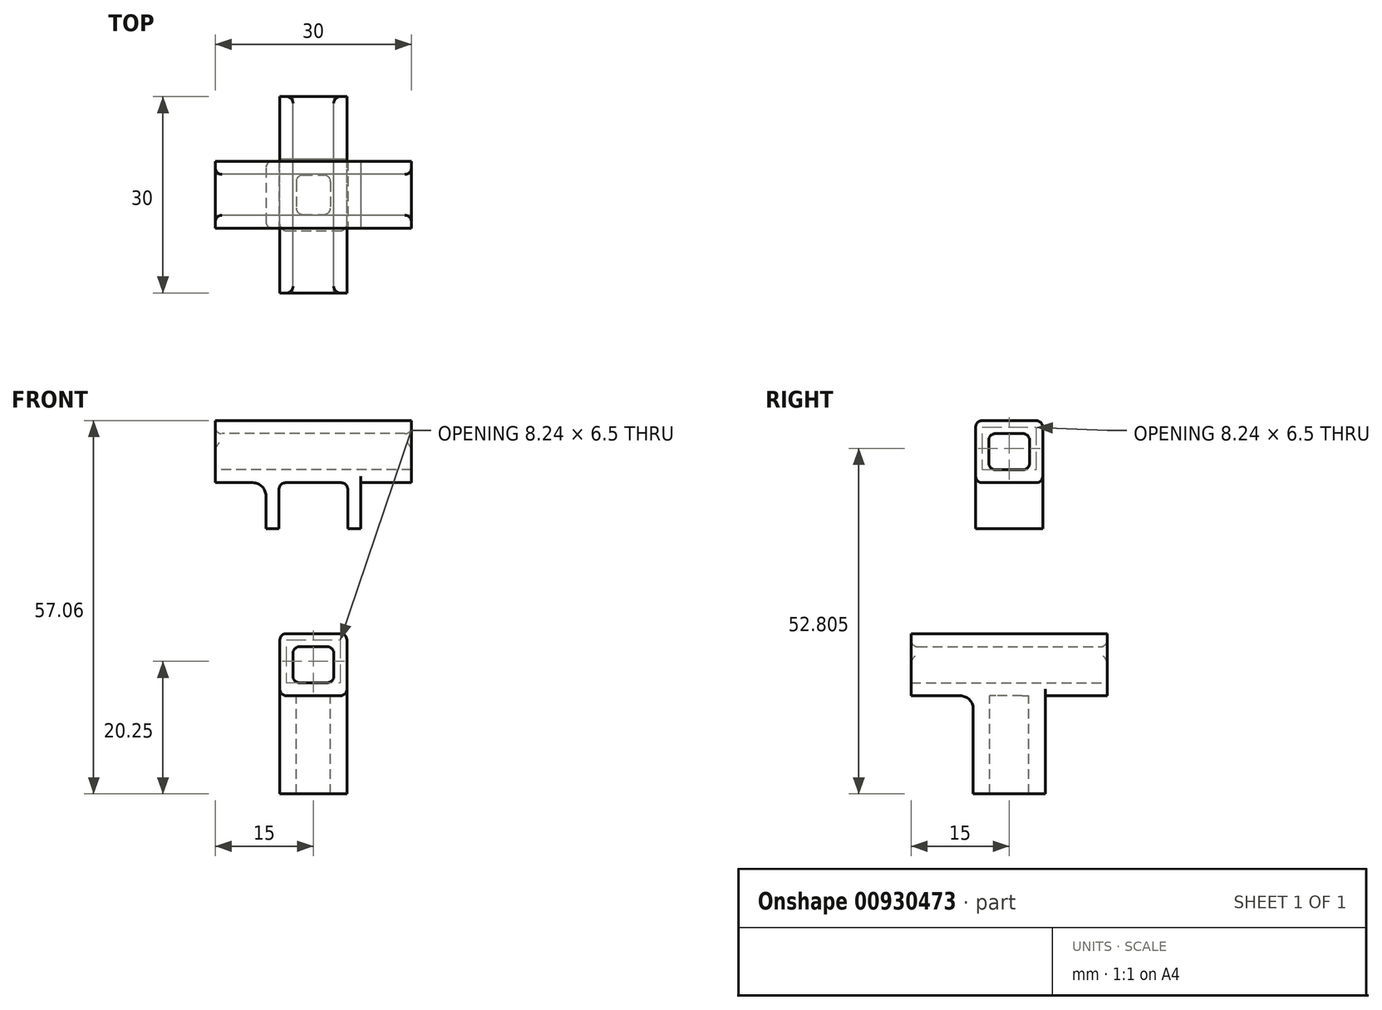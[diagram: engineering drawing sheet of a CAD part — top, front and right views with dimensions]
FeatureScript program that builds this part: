
annotation { "Feature Type Name" : "Feature", "Feature Type Description" : "" }
export const myFeature = defineFeature(function(context is Context, id is Id, definition is map)
    precondition{}
    {
        {
            var Q0;
            Q0=qCreatedBy(makeId("Front.planeOp"),FACE);
            var sketch = newSketch(context, id + "F0", { "sketchPlane" : qUnion([Q0])});
            skLineSegment(sketch, "E0.bottom", {"start": v(3.13, -2.75) * mm, "end": v(-3.12, -2.75) * mm});
            skLineSegment(sketch, "E0.top", {"start": v(3.12, 2.75) * mm, "end": v(-3.13, 2.75) * mm});
            skLineSegment(sketch, "E0.left", {"start": v(3.13, -2.75) * mm, "end": v(3.12, 2.75) * mm});
            skLineSegment(sketch, "E0.right", {"start": v(-3.12, -2.75) * mm, "end": v(-3.13, 2.75) * mm});
            skPoint(sketch, "E0.middle", {"position": v(0, 0) * mm});
            skLineSegment(sketch, "E1.0", {"start": v(5.12, 4.75) * mm, "end": v(-5.12, 4.75) * mm});
            skLineSegment(sketch, "E1.1", {"start": v(5.12, -4.75) * mm, "end": v(5.12, 4.75) * mm});
            skLineSegment(sketch, "E1.2", {"start": v(5.12, -4.75) * mm, "end": v(-5.12, -4.75) * mm});
            skLineSegment(sketch, "E1.3", {"start": v(-5.12, -4.75) * mm, "end": v(-5.12, 4.75) * mm});
            skSolve(sketch);
        }
        {
            var Q0;
            Q0=makeQuery(id+"F0.imprint","IMPRINT",FACE,{"disambiguationData":[TD([[makeQuery(id+"F0.imprint","IMPRINT",EDGE,{"derivedFrom":sQuery(id+"F0.wireOp",EDGE,"E0.bottom")}),1.0]])]});
            extrude(context, id + "F1", {"entities" : qUnion([Q0]), "endBound" : BoundingType.SYMMETRIC, "depth" : 30 * mm, "offsetDistance" : 25 * mm});
        }
        {
            var Q0;
            Q0=qCreatedBy(makeId("Right.planeOp"),FACE);
            var sketch = newSketch(context, id + "F2", { "sketchPlane" : qUnion([Q0])});
            skLineSegment(sketch, "E2.bottom", {"start": v(3.13, 4.8) * mm, "end": v(-3.13, 4.8) * mm});
            skLineSegment(sketch, "E2.top", {"start": v(3.13, 10.3) * mm, "end": v(-3.13, 10.3) * mm});
            skLineSegment(sketch, "E2.left", {"start": v(3.13, 4.8) * mm, "end": v(3.13, 10.3) * mm});
            skLineSegment(sketch, "E2.right", {"start": v(-3.13, 4.8) * mm, "end": v(-3.13, 10.3) * mm});
            skPoint(sketch, "E2.middle", {"position": v(0, 7.56) * mm});
            skLineSegment(sketch, "E3.0", {"start": v(5.13, 12.3) * mm, "end": v(-5.13, 12.3) * mm});
            skLineSegment(sketch, "E3.1", {"start": v(5.13, 2.8) * mm, "end": v(5.13, 12.3) * mm});
            skLineSegment(sketch, "E3.2", {"start": v(5.13, 2.8) * mm, "end": v(-5.13, 2.8) * mm});
            skLineSegment(sketch, "E3.3", {"start": v(-5.13, 2.8) * mm, "end": v(-5.13, 12.3) * mm});
            skSolve(sketch);
        }
        {
            var Q0;
            Q0=makeQuery(id+"F2.imprint","IMPRINT",FACE,{"disambiguationData":[TD([[makeQuery(id+"F2.imprint","IMPRINT",EDGE,{"derivedFrom":sQuery(id+"F2.wireOp",EDGE,"E2.bottom")}),1.0]])]});
            extrude(context, id + "F3", {"entities" : qUnion([Q0]), "endBound" : BoundingType.SYMMETRIC, "depth" : 30 * mm, "offsetDistance" : 25 * mm});
        }
        {
            var Q0;
            Q0=makeQuery(id+"F3.opExtrude","SWEPT_FACE",FACE,{"disambiguationData":[OSD([sQuery(id+"F2.wireOp",EDGE,"E3.2")])]});
            var sketch = newSketch(context, id + "F4", { "sketchPlane" : qUnion([Q0])});
            skLineSegment(sketch, "E4", {"start": v(0, 0) * mm, "end": v(-5.25, 0) * mm, "construction": true});
            skLineSegment(sketch, "E5.MirrorCS", {"start": v(0, 0) * mm, "end": v(5.25, 0) * mm, "construction": true});
            skLineSegment(sketch, "E6.bottom", {"start": v(-5.25, -5.13) * mm, "end": v(-7.25, -5.13) * mm});
            skLineSegment(sketch, "E6.top", {"start": v(-5.25, 5.13) * mm, "end": v(-7.25, 5.13) * mm});
            skLineSegment(sketch, "E6.left", {"start": v(-5.25, -5.13) * mm, "end": v(-5.25, 5.13) * mm});
            skLineSegment(sketch, "E6.right", {"start": v(-7.25, -5.13) * mm, "end": v(-7.25, 5.13) * mm});
            skLineSegment(sketch, "E7.MirrorCS", {"start": v(5.25, -5.13) * mm, "end": v(5.25, 5.13) * mm});
            skLineSegment(sketch, "E8.MirrorCS", {"start": v(7.25, -5.13) * mm, "end": v(7.25, 5.13) * mm});
            skLineSegment(sketch, "E9.MirrorCS", {"start": v(5.25, 5.13) * mm, "end": v(7.25, 5.13) * mm});
            skLineSegment(sketch, "E10.MirrorCS", {"start": v(5.25, -5.13) * mm, "end": v(7.25, -5.13) * mm});
            skSolve(sketch);
        }
        {
            var Q0;
            Q0=makeQuery(id+"F4.imprint","IMPRINT",FACE,{"disambiguationData":[TD([[makeQuery(id+"F4.imprint","IMPRINT",EDGE,{"derivedFrom":sQuery(id+"F4.wireOp",EDGE,"E6.top")}),1.0]])]});
            var Q1;
            Q1=makeQuery(id+"F4.imprint","IMPRINT",FACE,{"disambiguationData":[TD([[makeQuery(id+"F4.imprint","IMPRINT",EDGE,{"derivedFrom":sQuery(id+"F4.wireOp",EDGE,"E7.MirrorCS")}),-1.0]])]});
            extrude(context, id + "F5", {"entities" : qUnion([Q0, Q1]), "operationType" : NewBodyOperationType.ADD, "depth" : 7 * mm, "offsetDistance" : 25 * mm});
        }
        {
            var Q0;
            Q0=makeQuery(id+"F1.opExtrude","SWEPT_FACE",FACE,{"disambiguationData":[OSD([sQuery(id+"F0.wireOp",EDGE,"E1.2")])]});
            var sketch = newSketch(context, id + "F6", { "sketchPlane" : qUnion([Q0])});
            skLineSegment(sketch, "E11.bottom", {"start": v(-2.62, -3) * mm, "end": v(2.63, -3) * mm});
            skLineSegment(sketch, "E11.top", {"start": v(-2.63, 3) * mm, "end": v(2.62, 3) * mm});
            skLineSegment(sketch, "E11.left", {"start": v(-2.62, -3) * mm, "end": v(-2.63, 3) * mm});
            skLineSegment(sketch, "E11.right", {"start": v(2.63, -3) * mm, "end": v(2.62, 3) * mm});
            skPoint(sketch, "E11.middle", {"position": v(0, 0) * mm});
            skLineSegment(sketch, "E12.0", {"start": v(-5.12, -5.5) * mm, "end": v(5.12, -5.5) * mm});
            skLineSegment(sketch, "E12.1", {"start": v(-5.12, -5.5) * mm, "end": v(-5.13, 5.5) * mm});
            skLineSegment(sketch, "E12.2", {"start": v(-5.13, 5.5) * mm, "end": v(5.12, 5.5) * mm});
            skLineSegment(sketch, "E12.3", {"start": v(5.12, -5.5) * mm, "end": v(5.12, 5.5) * mm});
            skSolve(sketch);
        }
        {
            var Q0;
            Q0=makeQuery(id+"F6.imprint","IMPRINT",FACE,{"disambiguationData":[TD([[makeQuery(id+"F6.imprint","IMPRINT",EDGE,{"derivedFrom":sQuery(id+"F6.wireOp",EDGE,"E11.bottom")}),-1.0]])]});
            extrude(context, id + "F7", {"entities" : qUnion([Q0]), "operationType" : NewBodyOperationType.ADD, "depth" : 15 * mm, "offsetDistance" : 25 * mm});
        }
        {
            var Q0;
            Q0=makeQuery(id+"F5.opExtrude","CAP_EDGE",EDGE,{"disambiguationData":[OSD([sQuery(id+"F4.wireOp",EDGE,"E8.MirrorCS")])],"isStart":true});
            var Q1;
            Q1=makeQuery(id+"F5.opExtrude","CAP_EDGE",EDGE,{"disambiguationData":[OSD([sQuery(id+"F4.wireOp",EDGE,"E6.right")])],"isStart":true});
            fillet(context, id + "F8", {"entities" : qUnion([Q0, Q1]), "radius" : 2 * mm, "tangentPropagation" : true, "allowEdgeOverflow" : false});
        }
        {
            var Q0;
            Q0=makeQuery(id+"F7.opExtrude","CAP_EDGE",EDGE,{"disambiguationData":[OSD([sQuery(id+"F6.wireOp",EDGE,"E12.2")])],"isStart":true});
            var Q1;
            Q1=makeQuery(id+"F7.opExtrude","CAP_EDGE",EDGE,{"disambiguationData":[OSD([sQuery(id+"F6.wireOp",EDGE,"E12.0")])],"isStart":true});
            fillet(context, id + "F9", {"entities" : qUnion([Q0, Q1]), "radius" : 2 * mm, "tangentPropagation" : true, "allowEdgeOverflow" : false});
        }
        {
            var Q0;
            Q0=makeQuery(id+"F3.opExtrude","SWEPT_EDGE",EDGE,{"disambiguationData":[OSD([sQuery(id+"F2.wireOp",EDGE,"E2.top"),sQuery(id+"F2.wireOp",EDGE,"E2.right")])]});
            var Q1;
            Q1=makeQuery(id+"F3.opExtrude","SWEPT_EDGE",EDGE,{"disambiguationData":[OSD([sQuery(id+"F2.wireOp",EDGE,"E2.bottom"),sQuery(id+"F2.wireOp",EDGE,"E2.left")])]});
            var Q2;
            Q2=makeQuery(id+"F3.opExtrude","SWEPT_EDGE",EDGE,{"disambiguationData":[OSD([sQuery(id+"F2.wireOp",EDGE,"E2.bottom"),sQuery(id+"F2.wireOp",EDGE,"E2.right")])]});
            var Q3;
            Q3=makeQuery(id+"F3.opExtrude","SWEPT_EDGE",EDGE,{"disambiguationData":[OSD([sQuery(id+"F2.wireOp",EDGE,"E2.top"),sQuery(id+"F2.wireOp",EDGE,"E2.left")])]});
            var Q4;
            Q4=makeQuery(id+"F1.opExtrude","SWEPT_EDGE",EDGE,{"disambiguationData":[OSD([sQuery(id+"F0.wireOp",EDGE,"E0.top"),sQuery(id+"F0.wireOp",EDGE,"E0.left")])]});
            var Q5;
            Q5=makeQuery(id+"F1.opExtrude","SWEPT_EDGE",EDGE,{"disambiguationData":[OSD([sQuery(id+"F0.wireOp",EDGE,"E0.top"),sQuery(id+"F0.wireOp",EDGE,"E0.right")])]});
            var Q6;
            Q6=makeQuery(id+"F1.opExtrude","SWEPT_EDGE",EDGE,{"disambiguationData":[OSD([sQuery(id+"F0.wireOp",EDGE,"E0.bottom"),sQuery(id+"F0.wireOp",EDGE,"E0.right")])]});
            var Q7;
            Q7=makeQuery(id+"F1.opExtrude","SWEPT_EDGE",EDGE,{"disambiguationData":[OSD([sQuery(id+"F0.wireOp",EDGE,"E0.bottom"),sQuery(id+"F0.wireOp",EDGE,"E0.left")])]});
            var Q8;
            Q8=makeQuery(id+"F3.opExtrude","CAP_EDGE",EDGE,{"disambiguationData":[OSD([sQuery(id+"F2.wireOp",EDGE,"E2.top")])],"isStart":false});
            var Q9;
            Q9=makeQuery(id+"F3.opExtrude","CAP_EDGE",EDGE,{"disambiguationData":[OSD([sQuery(id+"F2.wireOp",EDGE,"E2.top")])],"isStart":true});
            var Q10;
            Q10=makeQuery(id+"F1.opExtrude","CAP_EDGE",EDGE,{"disambiguationData":[OSD([sQuery(id+"F0.wireOp",EDGE,"E0.top")])],"isStart":false});
            var Q11;
            Q11=makeQuery(id+"F1.opExtrude","CAP_EDGE",EDGE,{"disambiguationData":[OSD([sQuery(id+"F0.wireOp",EDGE,"E0.top")])],"isStart":true});
            fillet(context, id + "F10", {"entities" : qUnion([Q0, Q1, Q2, Q3, Q4, Q5, Q6, Q7, Q8, Q9, Q10, Q11]), "radius" : 1 * mm, "tangentPropagation" : true, "allowEdgeOverflow" : false});
        }
        {
            var Q0;
            Q0=makeQuery(id+"F3.opExtrude","SWEPT_EDGE",EDGE,{"disambiguationData":[OSD([sQuery(id+"F2.wireOp",EDGE,"E3.0"),sQuery(id+"F2.wireOp",EDGE,"E3.1")])]});
            var Q1;
            Q1=makeQuery(id+"F3.opExtrude","SWEPT_EDGE",EDGE,{"disambiguationData":[OSD([sQuery(id+"F2.wireOp",EDGE,"E3.0"),sQuery(id+"F2.wireOp",EDGE,"E3.3")])]});
            var Q2;
            Q2=makeQuery(id+"F1.opExtrude","SWEPT_EDGE",EDGE,{"disambiguationData":[OSD([sQuery(id+"F0.wireOp",EDGE,"E1.0"),sQuery(id+"F0.wireOp",EDGE,"E1.3")])]});
            var Q3;
            Q3=makeQuery(id+"F1.opExtrude","SWEPT_EDGE",EDGE,{"disambiguationData":[OSD([sQuery(id+"F0.wireOp",EDGE,"E1.0"),sQuery(id+"F0.wireOp",EDGE,"E1.1")])]});
            var Q4;
            Q4=makeQuery(id+"F5.opExtrude","CAP_EDGE",EDGE,{"disambiguationData":[OSD([sQuery(id+"F4.wireOp",EDGE,"E6.left")])],"isStart":true});
            var Q5;
            Q5=makeQuery(id+"F5.opExtrude","CAP_EDGE",EDGE,{"disambiguationData":[OSD([sQuery(id+"F4.wireOp",EDGE,"E7.MirrorCS")])],"isStart":true});
            fillet(context, id + "F11", {"entities" : qUnion([Q0, Q1, Q2, Q3, Q4, Q5]), "radius" : 1 * mm, "tangentPropagation" : true, "allowEdgeOverflow" : false});
        }
        {
            var Q0;
            {var subQ0=sQuery(id+"F2.wireOp",EDGE,"E3.2");var subQ1=sQuery(id+"F2.wireOp",EDGE,"E3.1");Q0=makeQuery(id+"F5.boolean.opBoolean","SPLIT",EDGE,{"disambiguationData":[TD([makeQuery(id+"F5.opExtrude","SWEPT_FACE",FACE,{"disambiguationData":[OSD([sQuery(id+"F4.wireOp",EDGE,"E6.right")])]})])],"derivedFrom":makeQuery(id+"F3.opExtrude","SWEPT_EDGE",EDGE,{"disambiguationData":[OSD([subQ1,subQ0])]})});}
            var Q1;
            {var subQ0=sQuery(id+"F2.wireOp",EDGE,"E3.2");var subQ1=sQuery(id+"F2.wireOp",EDGE,"E3.1");Q1=makeQuery(id+"F5.boolean.opBoolean","SPLIT",EDGE,{"disambiguationData":[TD([makeQuery(id+"F5.opExtrude","SWEPT_FACE",FACE,{"disambiguationData":[OSD([sQuery(id+"F4.wireOp",EDGE,"E8.MirrorCS")])]})])],"derivedFrom":makeQuery(id+"F3.opExtrude","SWEPT_EDGE",EDGE,{"disambiguationData":[OSD([subQ1,subQ0])]})});}
            var Q2;
            {var subQ0=sQuery(id+"F2.wireOp",EDGE,"E3.3");var subQ1=sQuery(id+"F2.wireOp",EDGE,"E3.2");Q2=makeQuery(id+"F5.boolean.opBoolean","SPLIT",EDGE,{"disambiguationData":[TD([makeQuery(id+"F5.opExtrude","SWEPT_FACE",FACE,{"disambiguationData":[OSD([sQuery(id+"F4.wireOp",EDGE,"E6.right")])]})])],"derivedFrom":makeQuery(id+"F3.opExtrude","SWEPT_EDGE",EDGE,{"disambiguationData":[OSD([subQ1,subQ0])]})});}
            var Q3;
            {var subQ0=sQuery(id+"F2.wireOp",EDGE,"E3.3");var subQ1=sQuery(id+"F2.wireOp",EDGE,"E3.2");Q3=makeQuery(id+"F5.boolean.opBoolean","SPLIT",EDGE,{"disambiguationData":[TD([makeQuery(id+"F5.opExtrude","SWEPT_FACE",FACE,{"disambiguationData":[OSD([sQuery(id+"F4.wireOp",EDGE,"E8.MirrorCS")])]})])],"derivedFrom":makeQuery(id+"F3.opExtrude","SWEPT_EDGE",EDGE,{"disambiguationData":[OSD([subQ1,subQ0])]})});}
            var Q4;
            Q4=makeQuery(id+"F1.opExtrude","SWEPT_EDGE",EDGE,{"disambiguationData":[OSD([sQuery(id+"F0.wireOp",EDGE,"E1.2"),sQuery(id+"F0.wireOp",EDGE,"E1.3")])]});
            var Q5;
            Q5=makeQuery(id+"F1.opExtrude","SWEPT_EDGE",EDGE,{"disambiguationData":[OSD([sQuery(id+"F0.wireOp",EDGE,"E1.1"),sQuery(id+"F0.wireOp",EDGE,"E1.2")])]});
            fillet(context, id + "F12", {"entities" : qUnion([Q0, Q1, Q2, Q3, Q4, Q5]), "radius" : 1 * mm, "tangentPropagation" : true, "allowEdgeOverflow" : false});
        }
        {
            var Q0;
            Q0=makeQuery(id+"F7.opExtrude","SWEPT_EDGE",EDGE,{"disambiguationData":[OSD([sQuery(id+"F6.wireOp",EDGE,"E11.top"),sQuery(id+"F6.wireOp",EDGE,"E11.left")])]});
            var Q1;
            Q1=makeQuery(id+"F7.opExtrude","SWEPT_EDGE",EDGE,{"disambiguationData":[OSD([sQuery(id+"F6.wireOp",EDGE,"E11.top"),sQuery(id+"F6.wireOp",EDGE,"E11.right")])]});
            var Q2;
            Q2=makeQuery(id+"F7.opExtrude","SWEPT_EDGE",EDGE,{"disambiguationData":[OSD([sQuery(id+"F6.wireOp",EDGE,"E11.bottom"),sQuery(id+"F6.wireOp",EDGE,"E11.right")])]});
            var Q3;
            Q3=makeQuery(id+"F7.opExtrude","SWEPT_EDGE",EDGE,{"disambiguationData":[OSD([sQuery(id+"F6.wireOp",EDGE,"E11.bottom"),sQuery(id+"F6.wireOp",EDGE,"E11.left")])]});
            fillet(context, id + "F13", {"entities" : qUnion([Q0, Q1, Q2, Q3]), "radius" : 1 * mm, "tangentPropagation" : true, "allowEdgeOverflow" : false});
        }
        {
            var Q0;
            Q0=makeQuery(id+"F3.opExtrude","SWEPT_BODY",BODY,{"disambiguationData":[OSD([sQuery(id+"F2.wireOp",EDGE,"E2.bottom"),sQuery(id+"F2.wireOp",EDGE,"E2.top"),sQuery(id+"F2.wireOp",EDGE,"E2.left"),sQuery(id+"F2.wireOp",EDGE,"E2.right"),sQuery(id+"F2.wireOp",EDGE,"E3.0"),sQuery(id+"F2.wireOp",EDGE,"E3.1"),sQuery(id+"F2.wireOp",EDGE,"E3.2"),sQuery(id+"F2.wireOp",EDGE,"E3.3")])]});
            var Q1;
            Q1=makeQuery(id+"F3.opExtrude","SWEPT_FACE",FACE,{"disambiguationData":[OSD([sQuery(id+"F2.wireOp",EDGE,"E3.0")])]});
            transform(context, id + "F14", {"entities" : qUnion([Q0]), "transformType" : TransformType.TRANSLATION_DISTANCE, "transformDirection" : qUnion([Q1]), "distance" : 25 * mm, "makeCopy" : false});
        }
    });
